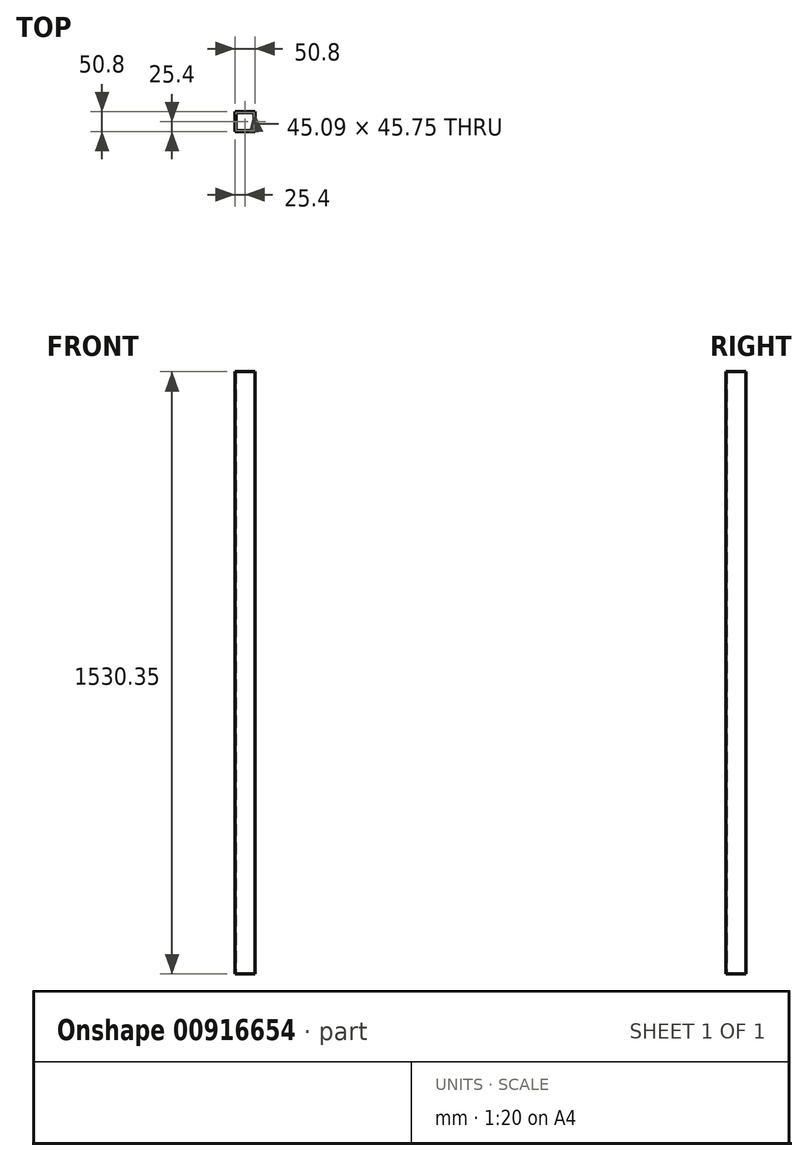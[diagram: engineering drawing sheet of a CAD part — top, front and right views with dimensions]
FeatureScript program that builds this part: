
annotation { "Feature Type Name" : "Feature", "Feature Type Description" : "" }
export const myFeature = defineFeature(function(context is Context, id is Id, definition is map)
    precondition{}
    {
        {
            var Q0;
            Q0=qCreatedBy(makeId("Top.planeOp"),FACE);
            var sketch = newSketch(context, id + "F0", { "sketchPlane" : qUnion([Q0])});
            skLineSegment(sketch, "E0.bottom", {"start": v(25.4, -25.4) * mm, "end": v(-25.4, -25.4) * mm});
            skLineSegment(sketch, "E0.top", {"start": v(25.4, 25.4) * mm, "end": v(-25.4, 25.4) * mm});
            skLineSegment(sketch, "E0.left", {"start": v(25.4, -25.4) * mm, "end": v(25.4, 25.4) * mm});
            skLineSegment(sketch, "E0.right", {"start": v(-25.4, -25.4) * mm, "end": v(-25.4, 25.4) * mm});
            skPoint(sketch, "E0.middle", {"position": v(0, 0) * mm});
            skLineSegment(sketch, "E1.left", {"start": v(22.35, 0) * mm, "end": v(22.35, 0) * mm});
            skLineSegment(sketch, "E1.right", {"start": v(-22.35, 0) * mm, "end": v(-22.35, 0) * mm});
            skLineSegment(sketch, "E2.bottom", {"start": v(22.55, 22.88) * mm, "end": v(-22.55, 22.88) * mm});
            skLineSegment(sketch, "E2.top", {"start": v(22.55, -22.88) * mm, "end": v(-22.55, -22.88) * mm});
            skLineSegment(sketch, "E2.left", {"start": v(22.55, 22.88) * mm, "end": v(22.55, -22.88) * mm});
            skLineSegment(sketch, "E2.right", {"start": v(-22.55, 22.88) * mm, "end": v(-22.55, -22.88) * mm});
            skSolve(sketch);
        }
        {
            var Q0;
            Q0 = qSketchRegion(id + "F0", true);
            extrude(context, id + "F1", {"entities" : qUnion([Q0]), "depth" : 1530.35 * mm, "offsetDistance" : 25.4 * mm});
        }
    });
